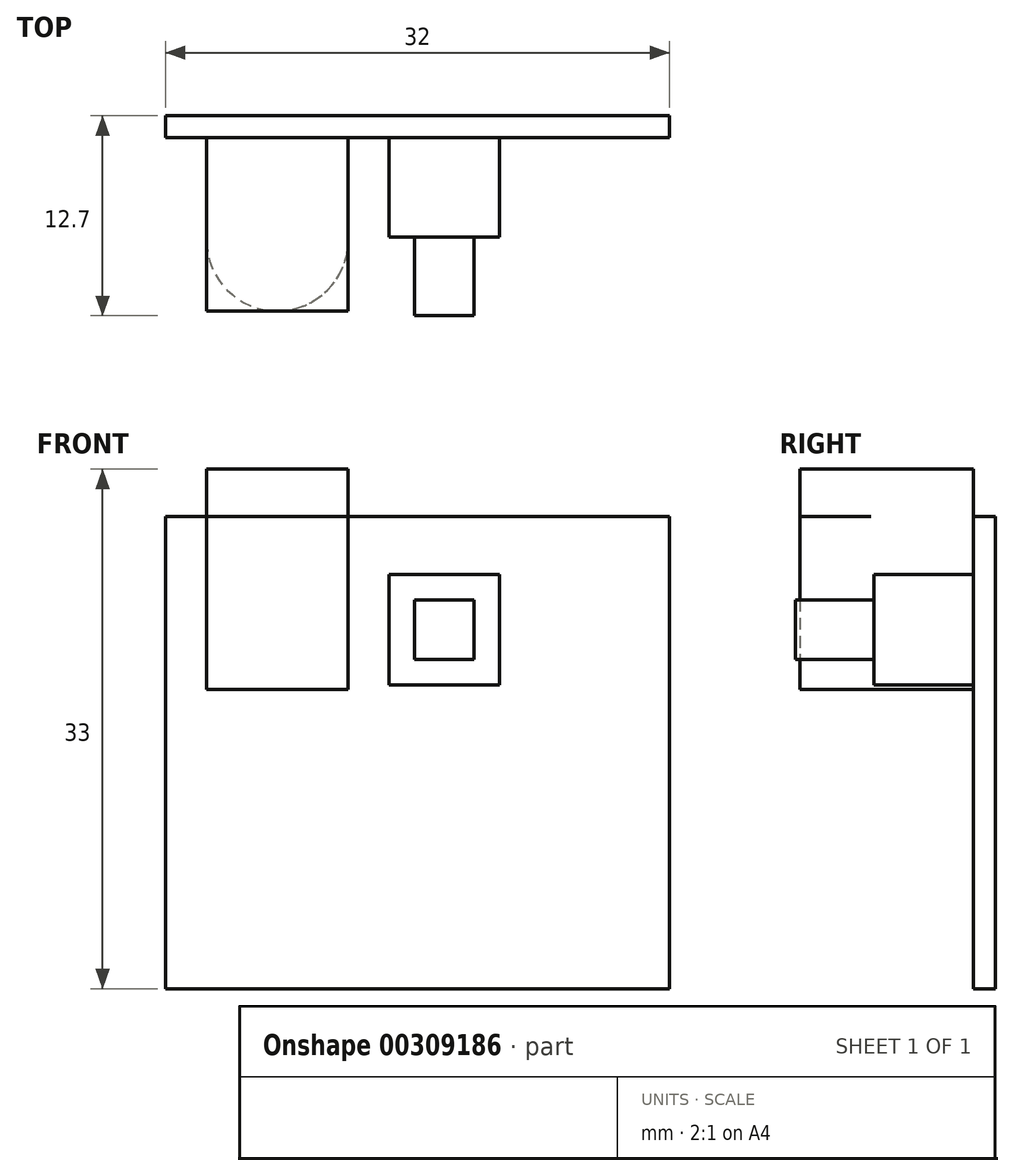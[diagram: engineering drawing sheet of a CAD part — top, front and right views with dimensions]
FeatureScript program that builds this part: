
annotation { "Feature Type Name" : "Feature", "Feature Type Description" : "" }
export const myFeature = defineFeature(function(context is Context, id is Id, definition is map)
    precondition{}
    {
        {
            var Q0;
            Q0=qCreatedBy(makeId("Front.planeOp"),FACE);
            var sketch = newSketch(context, id + "F0", { "sketchPlane" : qUnion([Q0])});
            skLineSegment(sketch, "E0.bottom", {"start": v(16, 15) * mm, "end": v(-16, 15) * mm});
            skLineSegment(sketch, "E0.top", {"start": v(16, -15) * mm, "end": v(-16, -15) * mm});
            skLineSegment(sketch, "E0.left", {"start": v(16, 15) * mm, "end": v(16, -15) * mm});
            skLineSegment(sketch, "E0.right", {"start": v(-16, 15) * mm, "end": v(-16, -15) * mm});
            skPoint(sketch, "E0.middle", {"position": v(0, 0) * mm});
            skSolve(sketch);
        }
        {
            var Q0;
            Q0=makeQuery(id+"F0.imprint","IMPRINT",FACE,{"disambiguationData":[TD([[makeQuery(id+"F0.imprint","IMPRINT",EDGE,{"derivedFrom":sQuery(id+"F0.wireOp",EDGE,"E0.bottom")}),1.0]])]});
            extrude(context, id + "F1", {"entities" : qUnion([Q0]), "depth" : 1.4 * mm});
        }
        {
            var Q0;
            Q0=makeQuery(id+"F1.opExtrude","CAP_FACE",FACE,{"disambiguationData":[OSD([sQuery(id+"F0.wireOp",EDGE,"E0.bottom"),sQuery(id+"F0.wireOp",EDGE,"E0.top"),sQuery(id+"F0.wireOp",EDGE,"E0.left"),sQuery(id+"F0.wireOp",EDGE,"E0.right")])],"isStart":false});
            var sketch = newSketch(context, id + "F2", { "sketchPlane" : qUnion([Q0])});
            skLineSegment(sketch, "E1.bottom", {"start": v(-13.4, 15) * mm, "end": v(-4.4, 15) * mm});
            skLineSegment(sketch, "E1.top", {"start": v(-13.4, 4) * mm, "end": v(-4.4, 4) * mm});
            skLineSegment(sketch, "E1.left", {"start": v(-13.4, 15) * mm, "end": v(-13.4, 4) * mm});
            skLineSegment(sketch, "E1.right", {"start": v(-4.4, 15) * mm, "end": v(-4.4, 4) * mm});
            skSolve(sketch);
        }
        {
            var Q0;
            Q0=qSketchRegion(id+"F2",true);
            extrude(context, id + "F3", {"entities" : qUnion([Q0]), "operationType" : NewBodyOperationType.ADD, "depth" : 11 * mm});
        }
        {
            var Q0;
            Q0=makeQuery(id+"F3.opExtrude","CAP_EDGE",EDGE,{"disambiguationData":[OSD([sQuery(id+"F2.wireOp",EDGE,"E1.right")])],"isStart":false});
            var Q1;
            Q1=makeQuery(id+"F3.opExtrude","CAP_EDGE",EDGE,{"disambiguationData":[OSD([sQuery(id+"F2.wireOp",EDGE,"E1.left")])],"isStart":false});
            fillet(context, id + "F4", {"entities" : qUnion([Q0, Q1]), "radius" : 4.5 * mm, "tangentPropagation" : true, "allowEdgeOverflow" : false});
        }
        {
            var Q0;
            Q0=makeQuery(id+"F3.boolean.opBoolean","MERGE",FACE,{"derivedFrom":[makeQuery(id+"F1.opExtrude","SWEPT_FACE",FACE,{"disambiguationData":[OSD([sQuery(id+"F0.wireOp",EDGE,"E0.bottom")])]}),makeQuery(id+"F3.opExtrude","SWEPT_FACE",FACE,{"disambiguationData":[OSD([sQuery(id+"F2.wireOp",EDGE,"E1.bottom")])]})]});
            var sketch = newSketch(context, id + "F5", { "sketchPlane" : qUnion([Q0])});
            skPoint(sketch, "E2.oppositeSnap0", {"position": v(-8.9, -12.4) * mm});
            skLineSegment(sketch, "E2.bottom", {"start": v(-4.4, -1.4) * mm, "end": v(-13.4, -1.4) * mm});
            skLineSegment(sketch, "E2.top", {"start": v(-4.4, -12.4) * mm, "end": v(-13.4, -12.4) * mm});
            skLineSegment(sketch, "E2.left", {"start": v(-4.4, -1.4) * mm, "end": v(-4.4, -12.4) * mm});
            skLineSegment(sketch, "E2.right", {"start": v(-13.4, -1.4) * mm, "end": v(-13.4, -12.4) * mm});
            skSolve(sketch);
        }
        {
            var Q0;
            Q0=makeQuery(id+"F1.opExtrude","CAP_FACE",FACE,{"disambiguationData":[OSD([sQuery(id+"F0.wireOp",EDGE,"E0.bottom"),sQuery(id+"F0.wireOp",EDGE,"E0.top"),sQuery(id+"F0.wireOp",EDGE,"E0.left"),sQuery(id+"F0.wireOp",EDGE,"E0.right")])],"isStart":false});
            var sketch = newSketch(context, id + "F6", { "sketchPlane" : qUnion([Q0])});
            skLineSegment(sketch, "E3.bottom", {"start": v(5.2, 11.3) * mm, "end": v(-1.8, 11.3) * mm});
            skLineSegment(sketch, "E3.top", {"start": v(5.2, 4.3) * mm, "end": v(-1.8, 4.3) * mm});
            skLineSegment(sketch, "E3.left", {"start": v(5.2, 11.3) * mm, "end": v(5.2, 4.3) * mm});
            skLineSegment(sketch, "E3.right", {"start": v(-1.8, 11.3) * mm, "end": v(-1.8, 4.3) * mm});
            skSolve(sketch);
        }
        {
            var Q0;
            Q0=makeQuery(id+"F6.imprint","IMPRINT",FACE,{"disambiguationData":[TD([[makeQuery(id+"F6.imprint","IMPRINT",EDGE,{"derivedFrom":sQuery(id+"F6.wireOp",EDGE,"E3.bottom")}),1.0]])]});
            extrude(context, id + "F7", {"entities" : qUnion([Q0]), "operationType" : NewBodyOperationType.ADD, "depth" : 6.3 * mm});
        }
        {
            var Q0;
            Q0=makeQuery(id+"F7.opExtrude","CAP_FACE",FACE,{"disambiguationData":[OSD([sQuery(id+"F6.wireOp",EDGE,"E3.bottom"),sQuery(id+"F6.wireOp",EDGE,"E3.top"),sQuery(id+"F6.wireOp",EDGE,"E3.left"),sQuery(id+"F6.wireOp",EDGE,"E3.right")])],"isStart":false});
            var sketch = newSketch(context, id + "F8", { "sketchPlane" : qUnion([Q0])});
            skLineSegment(sketch, "E4.bottom", {"start": v(3.6, 5.9) * mm, "end": v(-0.2, 5.9) * mm});
            skLineSegment(sketch, "E4.top", {"start": v(3.6, 9.7) * mm, "end": v(-0.2, 9.7) * mm});
            skLineSegment(sketch, "E4.left", {"start": v(3.6, 5.9) * mm, "end": v(3.6, 9.7) * mm});
            skLineSegment(sketch, "E4.right", {"start": v(-0.2, 5.9) * mm, "end": v(-0.2, 9.7) * mm});
            skPoint(sketch, "E4.middle", {"position": v(1.7, 7.8) * mm});
            skLineSegment(sketch, "E5", {"start": v(1.7, 11.3) * mm, "end": v(1.7, 4.3) * mm, "construction": true});
            skSolve(sketch);
        }
        {
            var Q0;
            Q0=qSketchRegion(id+"F8",true);
            extrude(context, id + "F9", {"entities" : qUnion([Q0]), "operationType" : NewBodyOperationType.ADD, "depth" : 5 * mm});
        }
        {
            var Q0;
            Q0=qSketchRegion(id+"F5",true);
            extrude(context, id + "F10", {"entities" : qUnion([Q0]), "operationType" : NewBodyOperationType.ADD, "depth" : 3 * mm});
        }
    });
